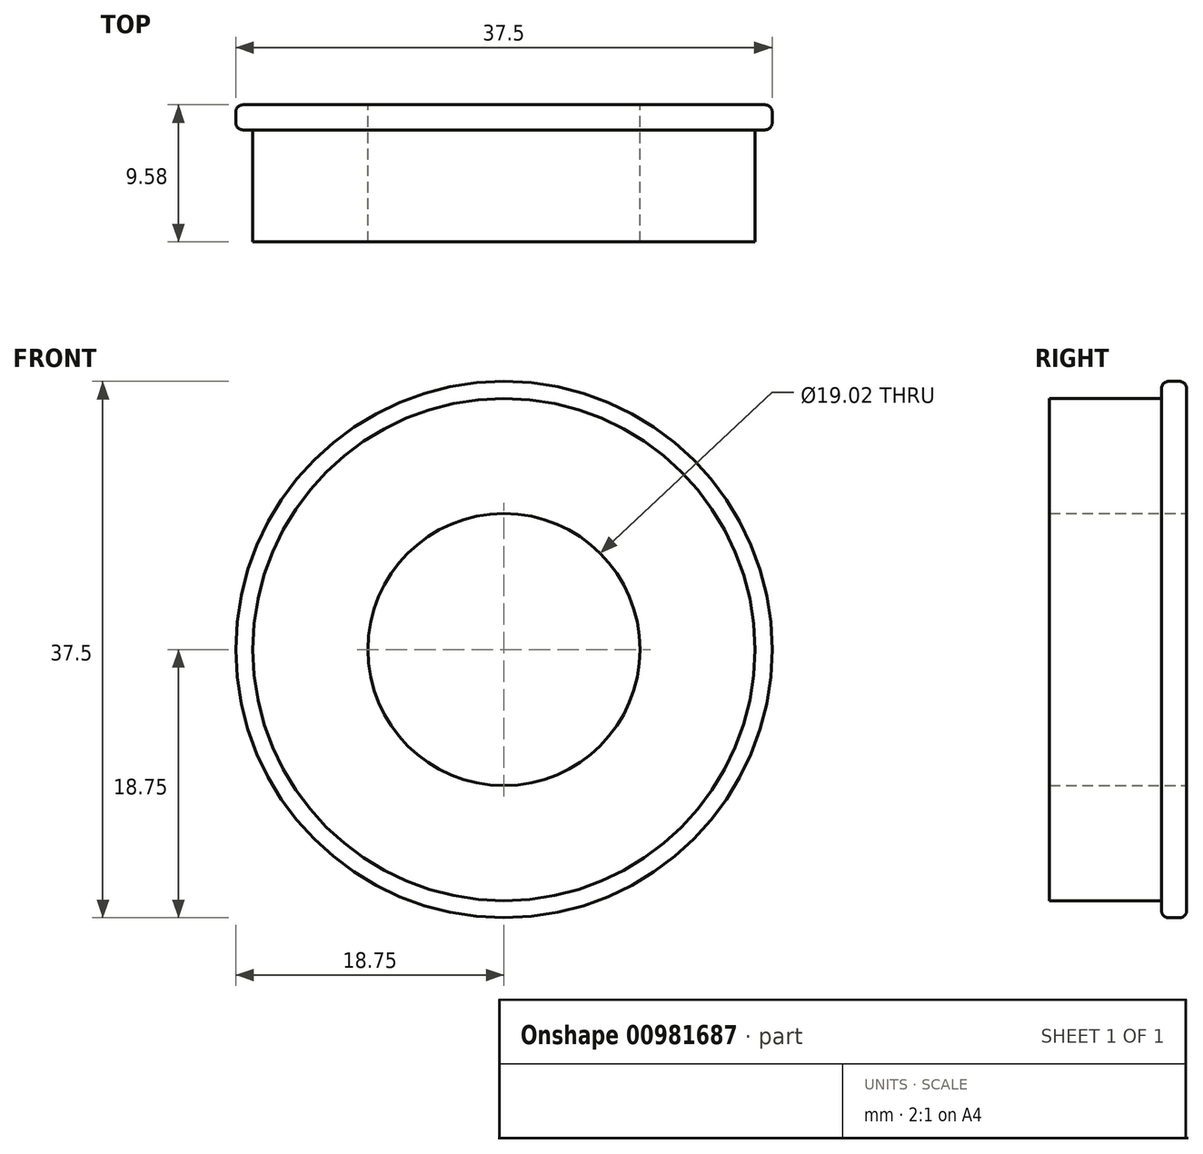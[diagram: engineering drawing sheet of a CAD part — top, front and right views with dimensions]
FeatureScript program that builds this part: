
annotation { "Feature Type Name" : "Feature", "Feature Type Description" : "" }
export const myFeature = defineFeature(function(context is Context, id is Id, definition is map)
    precondition{}
    {
        {
            var Q0;
            Q0=qCreatedBy(makeId("Front.planeOp"),FACE);
            var sketch = newSketch(context, id + "F0", { "sketchPlane" : qUnion([Q0])});
            skCircle(sketch, "E0", {"center": v(0, 0) * mm, "radius": 9.5 * mm});
            skCircle(sketch, "E1", {"center": v(0, 0) * mm, "radius": 17.55 * mm});
            skSolve(sketch);
        }
        {
            var Q0;
            Q0 = qSketchRegion(id + "F0", true);
            extrude(context, id + "F1", {"entities" : qUnion([Q0]), "depth" : 9.58 * mm, "offsetDistance" : 25 * mm});
        }
        {
            var Q0;
            Q0=qCreatedBy(makeId("Front.planeOp"),FACE);
            var sketch = newSketch(context, id + "F2", { "sketchPlane" : qUnion([Q0])});
            skCircle(sketch, "E2", {"center": v(0, 0) * mm, "radius": 18.75 * mm});
            skCircle(sketch, "E3.0", {"center": v(0, 0) * mm, "radius": 17.55 * mm});
            skSolve(sketch);
        }
        {
            var Q0;
            Q0 = qSketchRegion(id + "F2", true);
            extrude(context, id + "F3", {"entities" : qUnion([Q0]), "operationType" : NewBodyOperationType.ADD, "depth" : 1.75 * mm, "offsetDistance" : 25 * mm});
        }
        {
            var Q0;
            Q0=makeQuery(id+"F3.opExtrude","CAP_EDGE",EDGE,{"disambiguationData":[OSD([sQuery(id+"F2.wireOp",EDGE,"E2")])],"isStart":false});
            var Q1;
            Q1=makeQuery(id+"F3.opExtrude","CAP_EDGE",EDGE,{"disambiguationData":[OSD([sQuery(id+"F2.wireOp",EDGE,"E2")])],"isStart":true});
            fillet(context, id + "F4", {"entities" : qUnion([Q0, Q1]), "tangentPropagation" : true, "radius" : 0.5 * mm, "defaultsChanged" : true, "vertexSettings" : [], "allowEdgeOverflow" : false});
        }
    });
